# Revit family: 265-91-001 DN40-65
name_source: partatom
category: Pipe Accessories
units: mm (PartAtom-declared; Revit-internal decimal feet)

## family parameters
Always vertical = Yes
Cut with Voids When Loaded = No
Part Type = Valve - Breaks Into
Round Connector Dimension = Use Diameter
Shared = No
Work Plane-Based = No

## types (3) — shared parameters
25 = 25 mm  [stored 0.082021 ft]
Bolt.no = 4 mm  [stored 0.0131234 ft]
DN040_PN16 = 265-9-0040-10-14036400
DN050_PN16 = 265-9-0050-10-14036400
DN065_PN16 = 265-9-0065-10-14036400
Description_ = AVK DISMANTLING JOINT WITH CENTRE FLANGE, PN10/16
FL_T = 19 mm  [stored 0.062336 ft]
FL_T/2 = 10 mm  [stored 0.0328084 ft]
L3 = 10 mm  [stored 0.0328084 ft]
PN = 16 mm  [stored 0.0524934 ft]
Raised_dis = 3 mm  [stored 0.00984252 ft]
S = 16 mm  [stored 0.0524934 ft]
S11 = 22 mm
Search_table = 265-91-001 DN40-65
T = 6 mm  [stored 0.019685 ft]
T1 = 14 mm  [stored 0.0459318 ft]
URL_product_pages = https://www.avkvalves.com
zero-valued in all types: Default Elevation

## per-type parameters (varying)
| type | B1 | Bore | D | DN | L | L1 | L11 | L2 | PCD | raised_R |
| DN040_PN16 | 26 mm | 20 mm  [stored 0.0656168 ft] | 75 mm | 40 mm  [stored 0.131234 ft] | 325 mm  [stored 1.06627 ft] | 129 mm | 190 mm | 21 mm | 55 mm  [stored 0.180446 ft] | 49 mm |
| DN050_PN16 | 24 mm  [stored 0.0787402 ft] | 25 mm  [stored 0.082021 ft] | 83 mm | 50 mm  [stored 0.164042 ft] | 305 mm  [stored 1.00066 ft] | 122 mm | 180 mm  [stored 0.590551 ft] | 20 mm  [stored 0.0656168 ft] | 63 mm | 54 mm |
| DN065_PN16 | 24 mm  [stored 0.0787402 ft] | 33 mm  [stored 0.108268 ft] | 93 mm | 65 mm  [stored 0.213255 ft] | 305 mm  [stored 1.00066 ft] | 122 mm | 180 mm  [stored 0.590551 ft] | 20 mm  [stored 0.0656168 ft] | 73 mm | 60 mm |

note: [stored X ft] marks values corroborated as IEEE doubles in the binary element streams (Revit-internal decimal feet)

## geometry (parser evidence)
native form markers: Sweep x3
no freeform markers — native parametric forms only
